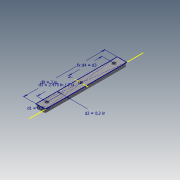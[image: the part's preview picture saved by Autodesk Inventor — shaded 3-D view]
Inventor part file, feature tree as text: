
AUTODESK INVENTOR PART (.ipt)
format: ipt  version: 2020.3 (Build 243373000, 373)  size: 110,592 bytes
history: native  units: in
note: dims shown in document units (in); Inventor stores cm internally (conversion verified against a paired STEP export)
features: fillet x2, sketch x1, extrude x1, hole x1
ambient origin geometry x8: Origin, YZ Plane, XZ Plane, XY Plane, X Axis, Y Axis, Z Axis, Center Point
bodies: Solid1 (feature_tree)
feature tree (5):
  sketch  "Sketch1"  dims[d0=3.0in d1=0.35in d2=0.2in d3=1.2375in d4=1.2375in d5=0.125in d6=0.0in d7=0.05in d8=0.05in d9=0.118in d10=0.75in d11=0.375in d12=0.25in d13=0.5635in d14=1.0in d15=0.8108in]
  extrude  "Extrusion1"  Depth=0.35in
  fillet  "Fillet1"  Radius=0.2in
  fillet  "Fillet2"  Radius=1.2375in
  hole  "Hole1"  [1 undecoded]
note: 1 required parameter value undecoded (feature->parameter linkage not recoverable at this tier; creation-order binding heuristic only, values carry confidence <= 0.55)
